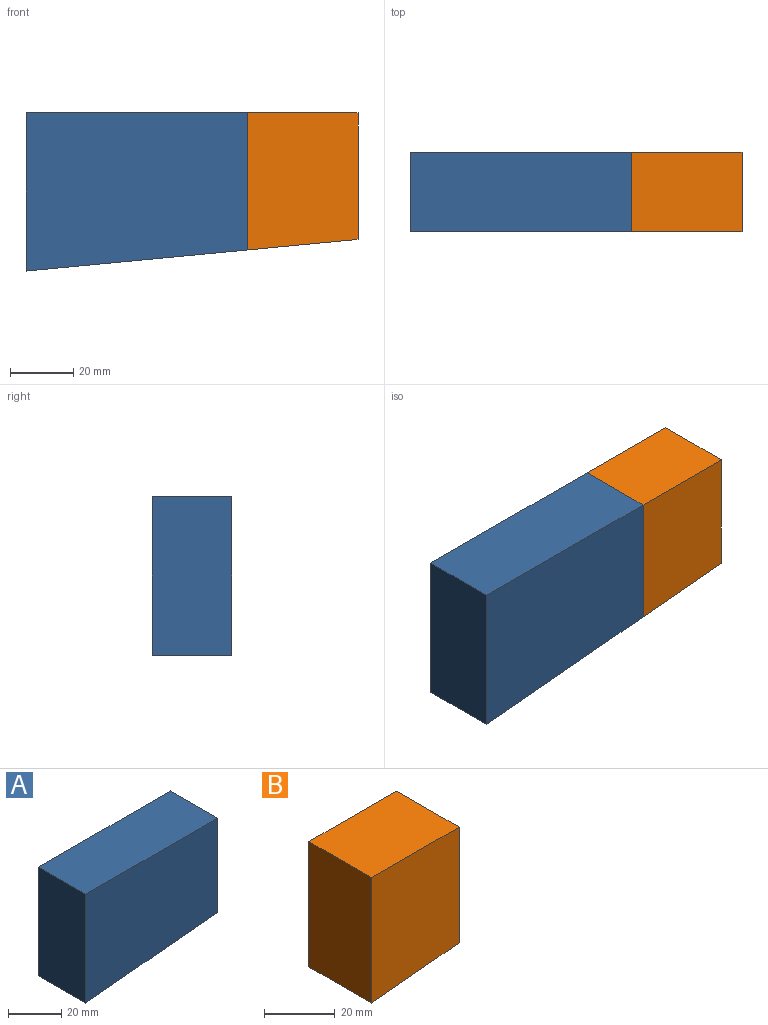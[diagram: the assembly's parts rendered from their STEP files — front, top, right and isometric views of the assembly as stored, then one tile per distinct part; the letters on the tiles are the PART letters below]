
ASSEMBLY  parts=2 mates=1
PART A: 6 faces, bbox 70x25x50 mm
  f0: plane 70x25mm, normal (0,0,1), area 1750mm2, adj f1,f3,f4,f5
  f1: plane 50x25mm, normal (-1,0,0), area 1250mm2, adj f0,f2,f4,f5
  f2: plane 70x25mm, normal (0.09,0,-1), area 1757.9mm2, adj f1,f3,f4,f5
  f3: plane 43.33x25mm, normal (1,0,0), area 1083.3mm2, adj f0,f2,f4,f5
  f4: plane 70x50mm, normal (0,-1,0), area 3266.7mm2, adj f0,f1,f2,f3
  f5: plane 70x50mm, normal (0,1,0), area 3266.7mm2, adj f0,f1,f2,f3
PART B: 6 faces, bbox 35x25x43.3 mm
  f0: plane 43.33x25mm, normal (-1,0,0), area 1083.3mm2, adj f1,f3,f4,f5
  f1: plane 35x25mm, normal (0.09,0,-1), area 879mm2, adj f0,f2,f4,f5
  f2: plane 40x25mm, normal (1,0,0), area 1000mm2, adj f1,f3,f4,f5
  f3: plane 35x25mm, normal (0,0,1), area 875mm2, adj f0,f2,f4,f5
  f4: plane 43.33x35mm, normal (0,-1,0), area 1458.3mm2, adj f0,f1,f2,f3
  f5: plane 43.33x35mm, normal (0,1,0), area 1458.3mm2, adj f0,f1,f2,f3
PLACE A at identity
PLACE B at identity
MATE revolute B.f4 <-> A.f4  axis (0,-1,0) through (70,-25,0)mm
